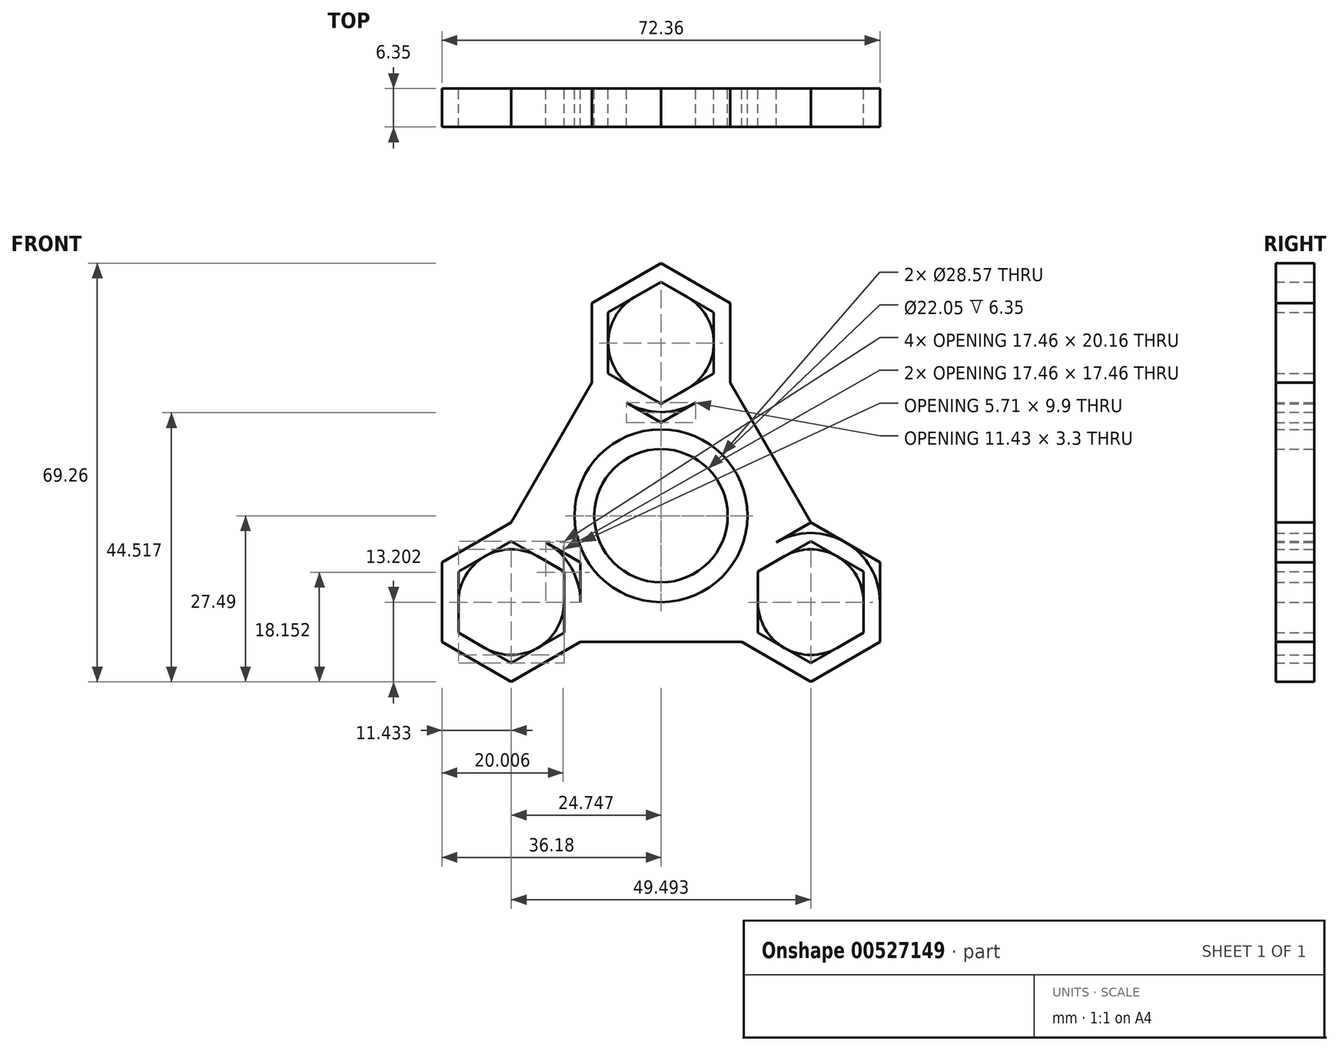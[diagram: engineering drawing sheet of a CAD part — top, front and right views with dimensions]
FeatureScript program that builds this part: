
annotation { "Feature Type Name" : "Feature", "Feature Type Description" : "" }
export const myFeature = defineFeature(function(context is Context, id is Id, definition is map)
    precondition{}
    {
        {
            var Q0;
            Q0=qCreatedBy(makeId("Front.planeOp"),FACE);
            var sketch = newSketch(context, id + "F0", { "sketchPlane" : qUnion([Q0])});
            skCircle(sketch, "E0", {"center": v(0, 0) * mm, "radius": 11.02 * mm});
            skCircle(sketch, "E1", {"center": v(0, 0) * mm, "radius": 14.29 * mm});
            skLineSegment(sketch, "E2.0", {"start": v(8.73, 33.62) * mm, "end": v(8.73, 23.53) * mm});
            skLineSegment(sketch, "E2.1", {"start": v(8.73, 23.53) * mm, "end": v(0, 18.5) * mm});
            skLineSegment(sketch, "E2.2", {"start": v(0, 18.5) * mm, "end": v(-8.73, 23.53) * mm});
            skLineSegment(sketch, "E2.3", {"start": v(-8.73, 23.53) * mm, "end": v(-8.73, 33.62) * mm});
            skLineSegment(sketch, "E2.4", {"start": v(-8.73, 33.62) * mm, "end": v(0, 38.66) * mm});
            skLineSegment(sketch, "E2.5", {"start": v(0, 38.66) * mm, "end": v(8.73, 33.62) * mm});
            skPoint(sketch, "E2.0.midPoint", {"position": v(8.73, 28.57) * mm});
            skPoint(sketch, "E3.cCircle.perimeterSnap0", {"position": v(-8.73, 28.57) * mm});
            skLineSegment(sketch, "E3.0", {"start": v(-11.43, 21.98) * mm, "end": v(-11.43, 35.17) * mm});
            skLineSegment(sketch, "E3.1", {"start": v(-11.43, 35.17) * mm, "end": v(0, 41.77) * mm});
            skLineSegment(sketch, "E3.2", {"start": v(0, 41.77) * mm, "end": v(11.43, 35.17) * mm});
            skLineSegment(sketch, "E3.3", {"start": v(11.43, 35.17) * mm, "end": v(11.43, 21.98) * mm});
            skLineSegment(sketch, "E3.4", {"start": v(11.43, 21.98) * mm, "end": v(0, 15.38) * mm});
            skLineSegment(sketch, "E3.5", {"start": v(0, 15.38) * mm, "end": v(-11.43, 21.98) * mm});
            skPoint(sketch, "E3.0.midPoint", {"position": v(-11.43, 28.57) * mm});
            skPoint(sketch, "E3.0.midPoint.positionSnap0", {"position": v(-8.73, 28.57) * mm});
            skPoint(sketch, "E4.1.0", {"position": v(-19.03, -24.19) * mm});
            skPoint(sketch, "E4.1.1", {"position": v(-20.38, -21.85) * mm});
            skLineSegment(sketch, "E4.1.4", {"start": v(-24.75, -27.49) * mm, "end": v(-36.18, -20.89) * mm});
            skLineSegment(sketch, "E4.1.5", {"start": v(-36.18, -20.89) * mm, "end": v(-36.18, -7.69) * mm});
            skPoint(sketch, "E4.1.6", {"position": v(-29.11, -6.73) * mm});
            skPoint(sketch, "E4.1.7", {"position": v(-20.38, -21.85) * mm});
            skLineSegment(sketch, "E4.1.8", {"start": v(-33.48, -9.25) * mm, "end": v(-24.75, -4.2) * mm});
            skLineSegment(sketch, "E4.1.9", {"start": v(-24.75, -4.2) * mm, "end": v(-16.02, -9.25) * mm});
            skLineSegment(sketch, "E4.1.10", {"start": v(-16.02, -9.25) * mm, "end": v(-16.02, -19.33) * mm});
            skLineSegment(sketch, "E4.1.11", {"start": v(-24.75, -24.37) * mm, "end": v(-33.48, -19.33) * mm});
            skLineSegment(sketch, "E4.1.12", {"start": v(-33.48, -19.33) * mm, "end": v(-33.48, -9.25) * mm});
            skLineSegment(sketch, "E4.1.13", {"start": v(-36.18, -7.69) * mm, "end": v(-24.75, -1.09) * mm});
            skLineSegment(sketch, "E4.1.14", {"start": v(-24.75, -1.09) * mm, "end": v(-13.32, -7.69) * mm});
            skLineSegment(sketch, "E4.1.15", {"start": v(-13.32, -7.69) * mm, "end": v(-13.32, -20.89) * mm});
            skLineSegment(sketch, "E4.1.16", {"start": v(-16.02, -19.33) * mm, "end": v(-24.75, -24.37) * mm});
            skLineSegment(sketch, "E4.1.17", {"start": v(-13.32, -20.89) * mm, "end": v(-24.75, -27.49) * mm});
            skPoint(sketch, "E4.2.0", {"position": v(30.46, -4.39) * mm});
            skPoint(sketch, "E4.2.1", {"position": v(29.11, -6.73) * mm});
            skLineSegment(sketch, "E4.2.4", {"start": v(36.18, -7.69) * mm, "end": v(36.18, -20.89) * mm});
            skLineSegment(sketch, "E4.2.5", {"start": v(36.18, -20.89) * mm, "end": v(24.75, -27.49) * mm});
            skPoint(sketch, "E4.2.6", {"position": v(20.38, -21.85) * mm});
            skPoint(sketch, "E4.2.7", {"position": v(29.11, -6.73) * mm});
            skLineSegment(sketch, "E4.2.8", {"start": v(24.75, -24.37) * mm, "end": v(16.02, -19.33) * mm});
            skLineSegment(sketch, "E4.2.9", {"start": v(16.02, -19.33) * mm, "end": v(16.02, -9.25) * mm});
            skLineSegment(sketch, "E4.2.10", {"start": v(16.02, -9.25) * mm, "end": v(24.75, -4.2) * mm});
            skLineSegment(sketch, "E4.2.11", {"start": v(33.48, -9.25) * mm, "end": v(33.48, -19.33) * mm});
            skLineSegment(sketch, "E4.2.12", {"start": v(33.48, -19.33) * mm, "end": v(24.75, -24.37) * mm});
            skLineSegment(sketch, "E4.2.13", {"start": v(24.75, -27.49) * mm, "end": v(13.32, -20.89) * mm});
            skLineSegment(sketch, "E4.2.14", {"start": v(13.32, -20.89) * mm, "end": v(13.32, -7.69) * mm});
            skLineSegment(sketch, "E4.2.15", {"start": v(13.32, -7.69) * mm, "end": v(24.75, -1.09) * mm});
            skLineSegment(sketch, "E4.2.16", {"start": v(24.75, -4.2) * mm, "end": v(33.48, -9.25) * mm});
            skLineSegment(sketch, "E4.2.17", {"start": v(24.75, -1.09) * mm, "end": v(36.18, -7.69) * mm});
            skLineSegment(sketch, "E5", {"start": v(-11.43, 21.98) * mm, "end": v(-24.75, -1.09) * mm});
            skLineSegment(sketch, "E6", {"start": v(11.43, 21.98) * mm, "end": v(24.75, -1.09) * mm});
            skLineSegment(sketch, "E7", {"start": v(-13.32, -20.89) * mm, "end": v(13.32, -20.89) * mm});
            skSolve(sketch);
        }
        {
            var Q0;
            Q0=qCreatedBy(makeId("Front.planeOp"),FACE);
            var sketch = newSketch(context, id + "F1", { "sketchPlane" : qUnion([Q0])});
            skLineSegment(sketch, "E8.0", {"start": v(-36.18, -20.89) * mm, "end": v(-36.18, -7.69) * mm});
            skLineSegment(sketch, "E8.1", {"start": v(0, 18.5) * mm, "end": v(-8.73, 23.53) * mm});
            skLineSegment(sketch, "E8.2", {"start": v(8.73, 23.53) * mm, "end": v(0, 18.5) * mm});
            skCircle(sketch, "E8.3", {"center": v(0, 28.57) * mm, "radius": 8.73 * mm});
            skLineSegment(sketch, "E8.4", {"start": v(-24.75, -1.09) * mm, "end": v(-13.32, -7.69) * mm});
            skCircle(sketch, "E8.5", {"center": v(0, 0) * mm, "radius": 14.29 * mm});
            skCircle(sketch, "E8.6", {"center": v(0, 0) * mm, "radius": 11.02 * mm});
            skLineSegment(sketch, "E8.7", {"start": v(0, 15.38) * mm, "end": v(-11.43, 21.98) * mm});
            skLineSegment(sketch, "E8.8", {"start": v(11.43, 21.98) * mm, "end": v(0, 15.38) * mm});
            skLineSegment(sketch, "E8.9", {"start": v(11.43, 35.17) * mm, "end": v(11.43, 21.98) * mm});
            skLineSegment(sketch, "E8.10", {"start": v(16.02, -19.33) * mm, "end": v(16.02, -9.25) * mm});
            skLineSegment(sketch, "E8.11", {"start": v(-8.73, 33.62) * mm, "end": v(0, 38.66) * mm});
            skLineSegment(sketch, "E8.12", {"start": v(0, 38.66) * mm, "end": v(8.73, 33.62) * mm});
            skCircle(sketch, "E8.13", {"center": v(0, 28.57) * mm, "radius": 11.43 * mm});
            skLineSegment(sketch, "E8.14", {"start": v(-11.43, 21.98) * mm, "end": v(-11.43, 35.17) * mm});
            skLineSegment(sketch, "E8.15", {"start": v(-11.43, 35.17) * mm, "end": v(0, 41.77) * mm});
            skLineSegment(sketch, "E8.16", {"start": v(0, 41.77) * mm, "end": v(11.43, 35.17) * mm});
            skLineSegment(sketch, "E8.17", {"start": v(-13.32, -7.69) * mm, "end": v(-13.32, -20.89) * mm});
            skLineSegment(sketch, "E8.18", {"start": v(24.75, -27.49) * mm, "end": v(13.32, -20.89) * mm});
            skLineSegment(sketch, "E8.19", {"start": v(-24.75, -24.37) * mm, "end": v(-33.48, -19.33) * mm});
            skLineSegment(sketch, "E8.20", {"start": v(16.02, -9.25) * mm, "end": v(24.75, -4.2) * mm});
            skLineSegment(sketch, "E8.21", {"start": v(-13.32, -20.89) * mm, "end": v(-24.75, -27.49) * mm});
            skCircle(sketch, "E8.22", {"center": v(-24.75, -14.29) * mm, "radius": 8.73 * mm});
            skLineSegment(sketch, "E8.23", {"start": v(36.18, -7.69) * mm, "end": v(36.18, -20.89) * mm});
            skLineSegment(sketch, "E8.24", {"start": v(13.32, -20.89) * mm, "end": v(13.32, -7.69) * mm});
            skLineSegment(sketch, "E8.25", {"start": v(-33.48, -19.33) * mm, "end": v(-33.48, -9.25) * mm});
            skLineSegment(sketch, "E8.26", {"start": v(-24.75, -4.2) * mm, "end": v(-16.02, -9.25) * mm});
            skLineSegment(sketch, "E8.27", {"start": v(33.48, -9.25) * mm, "end": v(33.48, -19.33) * mm});
            skCircle(sketch, "E8.28", {"center": v(-24.75, -14.29) * mm, "radius": 11.43 * mm});
            skLineSegment(sketch, "E8.29", {"start": v(36.18, -20.89) * mm, "end": v(24.75, -27.49) * mm});
            skLineSegment(sketch, "E8.30", {"start": v(13.32, -7.69) * mm, "end": v(24.75, -1.09) * mm});
            skLineSegment(sketch, "E8.31", {"start": v(-36.18, -7.69) * mm, "end": v(-24.75, -1.09) * mm});
            skLineSegment(sketch, "E8.32", {"start": v(-16.02, -9.25) * mm, "end": v(-16.02, -19.33) * mm});
            skCircle(sketch, "E8.33", {"center": v(24.75, -14.29) * mm, "radius": 11.43 * mm});
            skLineSegment(sketch, "E8.34", {"start": v(33.48, -19.33) * mm, "end": v(24.75, -24.37) * mm});
            skLineSegment(sketch, "E8.35", {"start": v(-24.75, -27.49) * mm, "end": v(-36.18, -20.89) * mm});
            skCircle(sketch, "E8.36", {"center": v(24.75, -14.29) * mm, "radius": 8.73 * mm});
            skLineSegment(sketch, "E9", {"start": v(-11.43, 21.98) * mm, "end": v(-24.75, -1.09) * mm});
            skLineSegment(sketch, "E10", {"start": v(11.43, 21.98) * mm, "end": v(24.75, -1.09) * mm});
            skLineSegment(sketch, "E11", {"start": v(-13.32, -20.89) * mm, "end": v(13.32, -20.89) * mm});
            skSolve(sketch);
        }
        {
            var Q0;
            Q0 = qSketchRegion(id + "F1", true);
            var Q1;
            Q1=makeQuery(id+"F0.imprint","IMPRINT",FACE,{"disambiguationData":[TD([[makeQuery(id+"F0.imprint","IMPRINT",EDGE,{"derivedFrom":sQuery(id+"F0.wireOp",EDGE,"E0")}),-1.0]])]});
            extrude(context, id + "F2", {"entities" : qUnion([Q0, Q1]), "depth" : 6.35 * mm, "offsetDistance" : 25.4 * mm});
        }
        {
            var Q0;
            Q0 = qSketchRegion(id + "F0", true);
            extrude(context, id + "F3", {"entities" : qUnion([Q0]), "depth" : 6.35 * mm, "offsetDistance" : 25.4 * mm});
        }
    });
